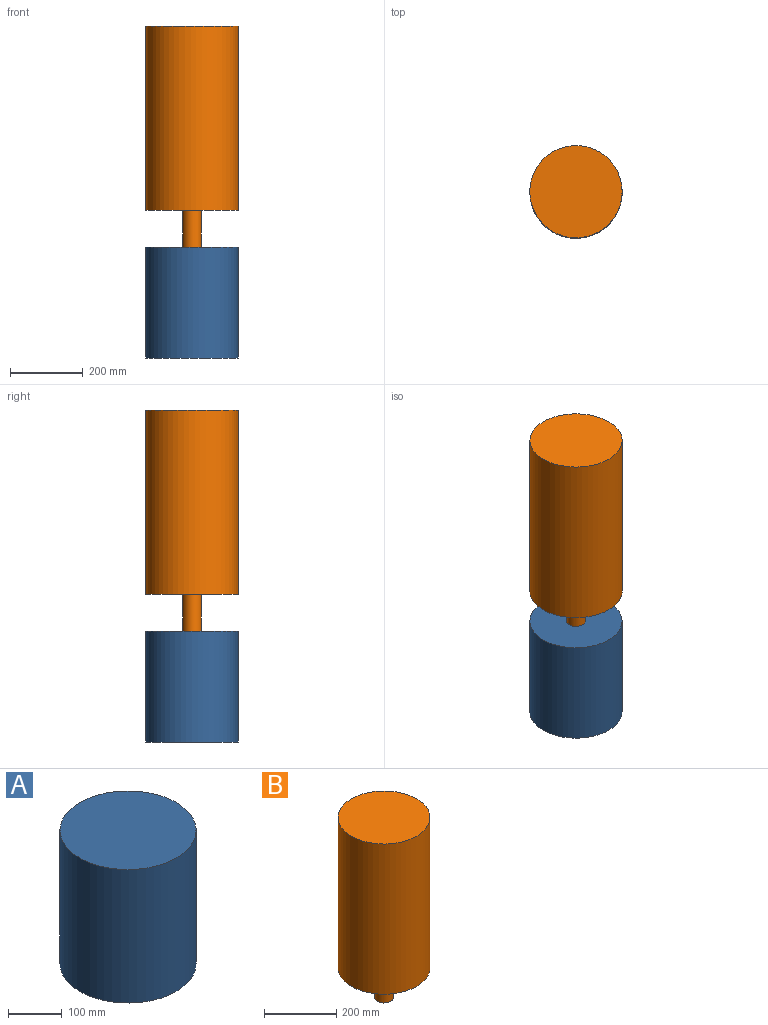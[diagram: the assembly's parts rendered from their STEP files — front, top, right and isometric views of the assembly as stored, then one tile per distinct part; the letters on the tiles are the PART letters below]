
ASSEMBLY  parts=2 mates=1
PART A: 3 faces, bbox 254x254x304.8 mm
  f0: cylinder r=127mm len=304.8mm, axis (0,0,-1), area 243219.6mm2, adj f1,f2
  f1: plane 254x254mm, normal (0,0,1), area 50670.7mm2, adj f0
  f2: plane 254x254mm, normal (0,0,-1), area 50670.7mm2, adj f0
PART B: 5 faces, bbox 254x254x609.6 mm
  f0: cylinder r=127mm len=508mm, axis (0,0,-1), area 405366mm2, adj f1,f3
  f1: plane 254x254mm, normal (0,0,1), area 50670.7mm2, adj f0
  f2: cylinder r=25.4mm len=101.6mm, axis (0,0,-1), area 16214.6mm2, adj f3,f4
  f3: plane 254x254mm, normal (0,0,-1), area 48643.9mm2, adj f0,f2
  f4: plane 50.8x50.8mm, normal (0,0,-1), area 2026.8mm2, adj f2
PLACE A rot(axis=(0,0,1),180deg) t=(-76.89,-6.63,1161.93)mm
PLACE B t=(-41.37,-51.63,1466.73)mm
MATE fastened A.f0 <-> B.f0  axis (0,0,1) through (-41.37,-6.2,1466.73)mm
